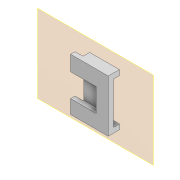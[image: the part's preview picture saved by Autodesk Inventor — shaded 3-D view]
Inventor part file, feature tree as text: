
AUTODESK INVENTOR PART (.ipt)
format: ipt  version: 2022 (Build 260153000, 153)  size: 155,648 bytes
history: native  units: in
note: dims shown in document units (in); Inventor stores cm internally (conversion verified against a paired STEP export)
features: other x5, sketch x4, extrude x4, projected_geometry x3, plane x2, reference x2
ambient origin geometry x8: Origin, YZ Plane, XZ Plane, XY Plane, X Axis, Y Axis, Z Axis, Center Point
bodies: Volumenkörper1 (feature_tree)
feature tree (20):
  plane  "Arbeitsebene1"
  sketch  "Skizze1"  dims[d0=0.0in d1=0.0197in]
  plane  "Arbeitsebene2"
  extrude  "Extrusion1"  Depth=0.0197in
  extrude  "Extrusion2"  Depth=0.0787in
  extrude  "Extrusion3"  Depth=0.3937in
  extrude  "Extrusion4"  TaperAngle=0.0deg  [1 undecoded]
  reference  "Referenz1"
  reference  "Referenz2"
  sketch  "Skizze2"  dims[d2=0.0197in d3=0.0787in]
  projected_geometry  "Projizierte Kontur1"
  sketch  "Skizze3"  dims[d4=0.0787in d5=0.3937in]
  projected_geometry  "Projizierte Kontur2"
  sketch  "Skizze4"  dims[d6=0.0197in d7=0.0in d8=0.3465in d9=0.3465in d10=0.0787in d11=0.0in d12=0.1181in d13=0.0984in d14=0.0in d15=0.0787in d16=0.0in]
  projected_geometry  "Projizierte Kontur3"
  other  "<userpath>\Documents\GitHub\Matchboxscope\INVENTOR\00_ESP3-CAM.iam"
  other  "00_ESP3-CAM.iam"
  other  "Bauteil50"
  other  "MicroSD Slot v1:1"
  other  "sdreader:1"
note: 1 required parameter value undecoded (feature->parameter linkage not recoverable at this tier; creation-order binding heuristic only, values carry confidence <= 0.55)
